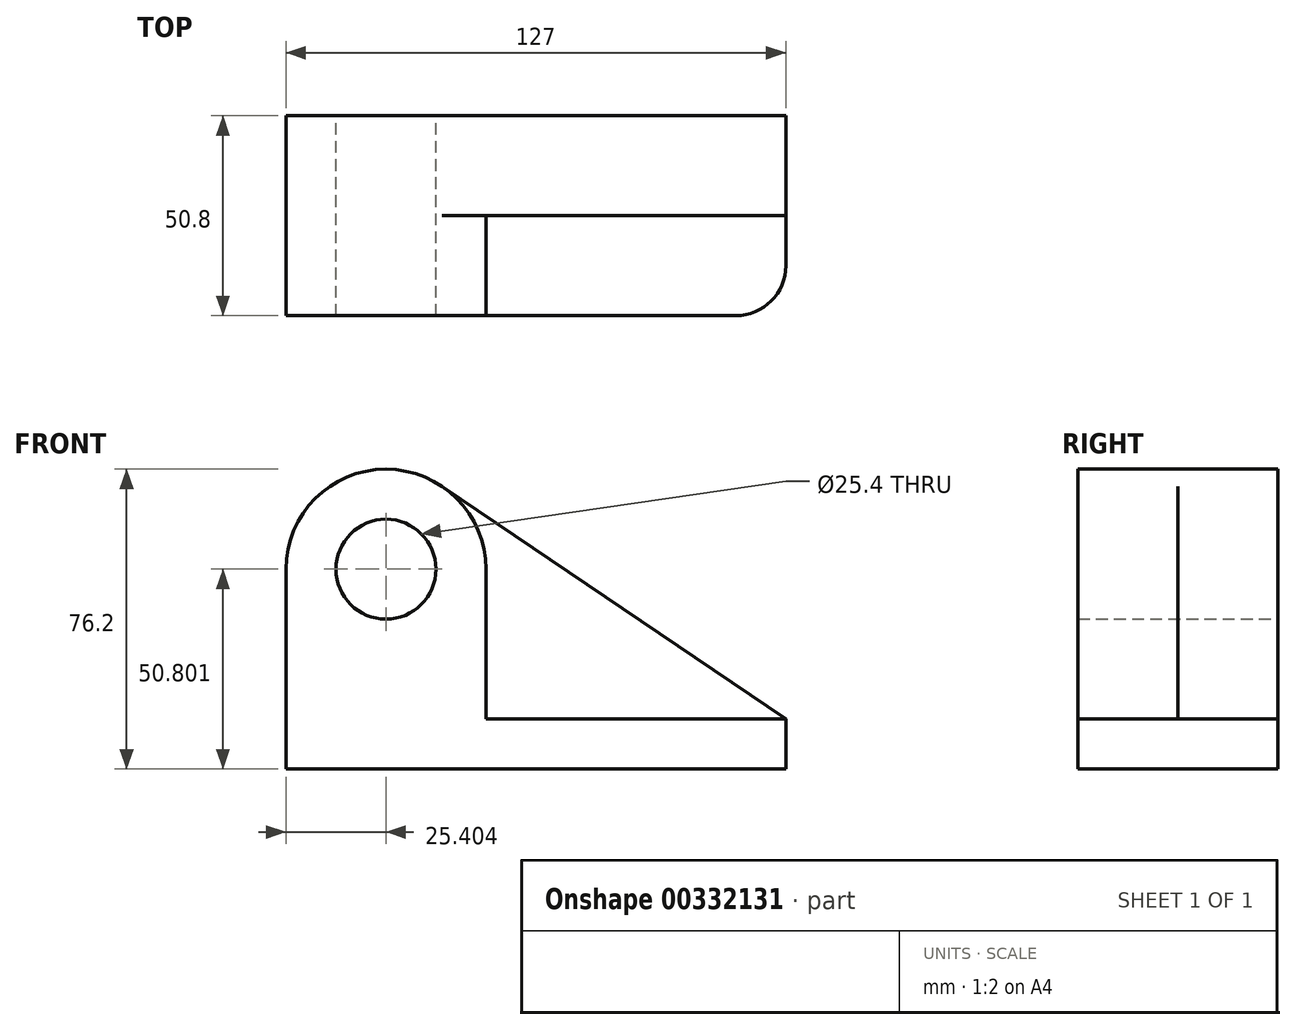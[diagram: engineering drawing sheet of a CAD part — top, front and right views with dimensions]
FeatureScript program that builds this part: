
annotation { "Feature Type Name" : "Feature", "Feature Type Description" : "" }
export const myFeature = defineFeature(function(context is Context, id is Id, definition is map)
    precondition{}
    {
        {
            var Q0;
            Q0=qCreatedBy(makeId("Front.planeOp"),FACE);
            var sketch = newSketch(context, id + "F0", { "sketchPlane" : qUnion([Q0])});
            skCircle(sketch, "E0", {"center": v(-36.53, 22.9) * mm, "radius": 12.7 * mm});
            skArc(sketch, "E1", {"start": v(-22.29, 43.94) * mm, "mid": v(-48.43, 45.34) * mm, "end": v(-61.93, 22.9) * mm});
            skLineSegment(sketch, "E2", {"start": v(-61.93, 22.9) * mm, "end": v(-61.93, -27.9) * mm});
            skLineSegment(sketch, "E3", {"start": v(-61.93, -27.9) * mm, "end": v(65.07, -27.9) * mm});
            skLineSegment(sketch, "E4", {"start": v(65.07, -27.9) * mm, "end": v(65.07, -15.2) * mm});
            skPoint(sketch, "E5.startSnap0", {"position": v(65.07, -21.55) * mm});
            skLineSegment(sketch, "E6", {"start": v(65.07, -15.2) * mm, "end": v(-22.29, 43.94) * mm});
            skSolve(sketch);
        }
        {
            var Q0;
            Q0=makeQuery(id+"F0.imprint","IMPRINT",FACE,{"disambiguationData":[TD([[makeQuery(id+"F0.imprint","IMPRINT",EDGE,{"derivedFrom":sQuery(id+"F0.wireOp",EDGE,"E0")}),-1.0]])]});
            extrude(context, id + "F1", {"entities" : qUnion([Q0]), "depth" : 25.4 * mm});
        }
        {
            var Q0;
            Q0=makeQuery(id+"F1.opExtrude","CAP_FACE",FACE,{"disambiguationData":[OSD([sQuery(id+"F0.wireOp",EDGE,"E0"),sQuery(id+"F0.wireOp",EDGE,"E1"),sQuery(id+"F0.wireOp",EDGE,"E2"),sQuery(id+"F0.wireOp",EDGE,"E3"),sQuery(id+"F0.wireOp",EDGE,"E4"),sQuery(id+"F0.wireOp",EDGE,"E6")])],"isStart":false});
            var sketch = newSketch(context, id + "F2", { "sketchPlane" : qUnion([Q0])});
            skCircle(sketch, "E7", {"center": v(-36.53, 22.9) * mm, "radius": 12.7 * mm});
            skArc(sketch, "E8", {"start": v(-11.13, 22.9) * mm, "mid": v(-36.53, 48.3) * mm, "end": v(-61.93, 22.9) * mm});
            skLineSegment(sketch, "E9.bottom", {"start": v(65.07, -15.2) * mm, "end": v(-11.13, -15.2) * mm});
            skLineSegment(sketch, "E9.top", {"start": v(65.07, -27.9) * mm, "end": v(-61.93, -27.9) * mm});
            skLineSegment(sketch, "E9.left", {"start": v(65.07, -15.2) * mm, "end": v(65.07, -27.9) * mm});
            skLineSegment(sketch, "E9.right", {"start": v(-61.93, -15.2) * mm, "end": v(-61.93, -27.9) * mm});
            skLineSegment(sketch, "E10", {"start": v(-11.13, 22.9) * mm, "end": v(-11.13, -15.2) * mm});
            skLineSegment(sketch, "E11", {"start": v(-61.93, 22.9) * mm, "end": v(-61.93, -15.2) * mm});
            skSolve(sketch);
        }
        {
            var Q0;
            Q0=makeQuery(id+"F2.imprint","IMPRINT",FACE,{"disambiguationData":[TD([[makeQuery(id+"F2.imprint","IMPRINT",EDGE,{"derivedFrom":sQuery(id+"F2.wireOp",EDGE,"E7")}),-1.0]])]});
            extrude(context, id + "F3", {"entities" : qUnion([Q0]), "operationType" : NewBodyOperationType.ADD, "depth" : 25.4 * mm});
        }
        {
            var Q0;
            Q0=makeQuery(id+"F3.opExtrude","CAP_EDGE",EDGE,{"disambiguationData":[OSD([sQuery(id+"F2.wireOp",EDGE,"E9.left")])],"isStart":false});
            fillet(context, id + "F4", {"entities" : qUnion([Q0]), "radius" : 12.7 * mm, "tangentPropagation" : true, "allowEdgeOverflow" : false});
        }
    });
